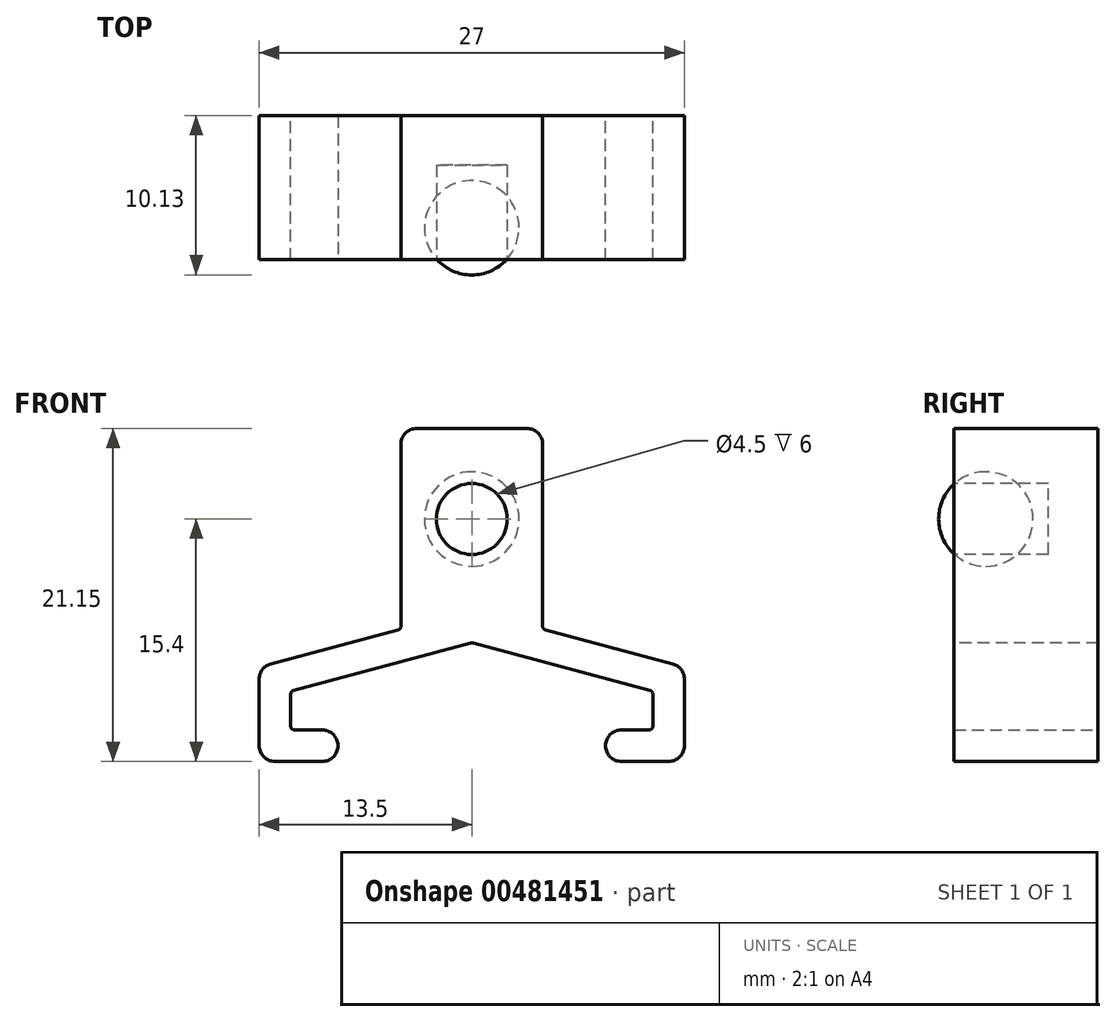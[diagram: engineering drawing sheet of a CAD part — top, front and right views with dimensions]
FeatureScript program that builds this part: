
annotation { "Feature Type Name" : "Feature", "Feature Type Description" : "" }
export const myFeature = defineFeature(function(context is Context, id is Id, definition is map)
    precondition{}
    {
        {
            var Q0;
            Q0=qCreatedBy(makeId("Front.planeOp"),FACE);
            var sketch = newSketch(context, id + "F0", { "sketchPlane" : qUnion([Q0])});
            skLineSegment(sketch, "E0.bottom", {"start": v(-13.5, -3) * mm, "end": v(-8.5, -3) * mm});
            skLineSegment(sketch, "E0.left", {"start": v(-13.5, -3) * mm, "end": v(-13.5, 3) * mm});
            skLineSegment(sketch, "E0.right", {"start": v(13.5, -3) * mm, "end": v(13.5, 3) * mm});
            skPoint(sketch, "E0.middle", {"position": v(0, 0) * mm});
            skLineSegment(sketch, "E1.top", {"start": v(4.5, 18.15) * mm, "end": v(-4.5, 18.15) * mm});
            skLineSegment(sketch, "E1.left", {"start": v(4.5, 5.4) * mm, "end": v(4.5, 18.15) * mm});
            skLineSegment(sketch, "E1.right", {"start": v(-4.5, 5.4) * mm, "end": v(-4.5, 18.15) * mm});
            skPoint(sketch, "E1.middle", {"position": v(0, 11.78) * mm});
            skLineSegment(sketch, "E2", {"start": v(4.5, 5.4) * mm, "end": v(13.5, 3) * mm});
            skLineSegment(sketch, "E3", {"start": v(-13.5, 3) * mm, "end": v(-4.5, 5.4) * mm});
            skLineSegment(sketch, "E4.0", {"start": v(-11.5, -1) * mm, "end": v(-8.5, -1) * mm});
            skLineSegment(sketch, "E5.0", {"start": v(-11.5, -1) * mm, "end": v(-11.5, 1.46) * mm});
            skLineSegment(sketch, "E6.0", {"start": v(-11.5, 1.46) * mm, "end": v(0, 4.53) * mm});
            skLineSegment(sketch, "E7.0", {"start": v(0, 4.53) * mm, "end": v(11.5, 1.46) * mm});
            skLineSegment(sketch, "E8.0", {"start": v(11.5, -1) * mm, "end": v(11.5, 1.46) * mm});
            skLineSegment(sketch, "E9", {"start": v(-8.5, -1) * mm, "end": v(-8.5, -3) * mm});
            skLineSegment(sketch, "E10.MirrorCS", {"start": v(8.5, -1) * mm, "end": v(8.5, -3) * mm});
            skLineSegment(sketch, "E11.trimOffspring", {"start": v(8.5, -1) * mm, "end": v(11.5, -1) * mm});
            skLineSegment(sketch, "E12.trimOffspring", {"start": v(8.5, -3) * mm, "end": v(13.5, -3) * mm});
            skSolve(sketch);
        }
        {
            var Q0;
            Q0=makeQuery(id+"F0.imprint","IMPRINT",FACE,{"disambiguationData":[TD([[makeQuery(id+"F0.imprint","IMPRINT",EDGE,{"derivedFrom":sQuery(id+"F0.wireOp",EDGE,"E0.bottom")}),1.0]])]});
            extrude(context, id + "F1", {"entities" : qUnion([Q0]), "depth" : 4.58 * mm, "hasSecondDirection" : true, "secondDirectionOppositeDirection" : true, "secondDirectionDepth" : 4.58 * mm});
        }
        {
            var Q0;
            Q0=makeQuery(id+"F1.opExtrude","CAP_FACE",FACE,{"disambiguationData":[OSD([sQuery(id+"F0.wireOp",EDGE,"E0.bottom"),sQuery(id+"F0.wireOp",EDGE,"E0.left"),sQuery(id+"F0.wireOp",EDGE,"E0.right"),sQuery(id+"F0.wireOp",EDGE,"E1.top"),sQuery(id+"F0.wireOp",EDGE,"E1.left"),sQuery(id+"F0.wireOp",EDGE,"E1.right"),sQuery(id+"F0.wireOp",EDGE,"E2"),sQuery(id+"F0.wireOp",EDGE,"E3"),sQuery(id+"F0.wireOp",EDGE,"E4.0"),sQuery(id+"F0.wireOp",EDGE,"E5.0"),sQuery(id+"F0.wireOp",EDGE,"E6.0"),sQuery(id+"F0.wireOp",EDGE,"E7.0"),sQuery(id+"F0.wireOp",EDGE,"E8.0"),sQuery(id+"F0.wireOp",EDGE,"E9"),sQuery(id+"F0.wireOp",EDGE,"E10.MirrorCS"),sQuery(id+"F0.wireOp",EDGE,"E11.trimOffspring"),sQuery(id+"F0.wireOp",EDGE,"E12.trimOffspring")])],"isStart":false});
            var sketch = newSketch(context, id + "F2", { "sketchPlane" : qUnion([Q0])});
            skCircle(sketch, "E13", {"center": v(0, 12.4) * mm, "radius": 2.25 * mm});
            skSolve(sketch);
        }
        {
            var Q0;
            Q0=makeQuery(id+"F2.imprint","IMPRINT",FACE,{"disambiguationData":[TD([[makeQuery(id+"F2.imprint","IMPRINT",EDGE,{"derivedFrom":sQuery(id+"F2.wireOp",EDGE,"E13")}),1.0]])]});
            extrude(context, id + "F3", {"entities" : qUnion([Q0]), "operationType" : NewBodyOperationType.REMOVE, "oppositeDirection" : true, "depth" : 6 * mm});
        }
        {
            var Q0;
            Q0=makeQuery(id+"F1.opExtrude","SWEPT_EDGE",EDGE,{"disambiguationData":[OSD([sQuery(id+"F0.wireOp",EDGE,"E1.top"),sQuery(id+"F0.wireOp",EDGE,"E1.right")])]});
            var Q1;
            Q1=makeQuery(id+"F1.opExtrude","SWEPT_EDGE",EDGE,{"disambiguationData":[OSD([sQuery(id+"F0.wireOp",EDGE,"E1.top"),sQuery(id+"F0.wireOp",EDGE,"E1.left")])]});
            var Q2;
            Q2=makeQuery(id+"F1.opExtrude","SWEPT_EDGE",EDGE,{"disambiguationData":[OSD([sQuery(id+"F0.wireOp",EDGE,"E0.right"),sQuery(id+"F0.wireOp",EDGE,"E2")])]});
            var Q3;
            Q3=makeQuery(id+"F1.opExtrude","SWEPT_EDGE",EDGE,{"disambiguationData":[OSD([sQuery(id+"F0.wireOp",EDGE,"E0.right"),sQuery(id+"F0.wireOp",EDGE,"E12.trimOffspring")])]});
            var Q4;
            Q4=makeQuery(id+"F1.opExtrude","SWEPT_EDGE",EDGE,{"disambiguationData":[OSD([sQuery(id+"F0.wireOp",EDGE,"E10.MirrorCS"),sQuery(id+"F0.wireOp",EDGE,"E12.trimOffspring")])]});
            var Q5;
            Q5=makeQuery(id+"F1.opExtrude","SWEPT_EDGE",EDGE,{"disambiguationData":[OSD([sQuery(id+"F0.wireOp",EDGE,"E10.MirrorCS"),sQuery(id+"F0.wireOp",EDGE,"E11.trimOffspring")])]});
            var Q6;
            Q6=makeQuery(id+"F1.opExtrude","SWEPT_EDGE",EDGE,{"disambiguationData":[OSD([sQuery(id+"F0.wireOp",EDGE,"E0.bottom"),sQuery(id+"F0.wireOp",EDGE,"E9")])]});
            var Q7;
            Q7=makeQuery(id+"F1.opExtrude","SWEPT_EDGE",EDGE,{"disambiguationData":[OSD([sQuery(id+"F0.wireOp",EDGE,"E4.0"),sQuery(id+"F0.wireOp",EDGE,"E9")])]});
            var Q8;
            Q8=makeQuery(id+"F1.opExtrude","SWEPT_EDGE",EDGE,{"disambiguationData":[OSD([sQuery(id+"F0.wireOp",EDGE,"E0.left"),sQuery(id+"F0.wireOp",EDGE,"E3")])]});
            var Q9;
            Q9=makeQuery(id+"F1.opExtrude","SWEPT_EDGE",EDGE,{"disambiguationData":[OSD([sQuery(id+"F0.wireOp",EDGE,"E0.bottom"),sQuery(id+"F0.wireOp",EDGE,"E0.left")])]});
            fillet(context, id + "F4", {"entities" : qUnion([Q0, Q1, Q2, Q3, Q4, Q5, Q6, Q7, Q8, Q9]), "radius" : 1 * mm, "tangentPropagation" : true, "allowEdgeOverflow" : false});
        }
        {
            var Q0;
            Q0=makeQuery(id+"F1.opExtrude","SWEPT_EDGE",EDGE,{"disambiguationData":[OSD([sQuery(id+"F0.wireOp",EDGE,"E1.left"),sQuery(id+"F0.wireOp",EDGE,"E2")])]});
            var Q1;
            Q1=makeQuery(id+"F1.opExtrude","SWEPT_EDGE",EDGE,{"disambiguationData":[OSD([sQuery(id+"F0.wireOp",EDGE,"E4.0"),sQuery(id+"F0.wireOp",EDGE,"E5.0")])]});
            var Q2;
            Q2=makeQuery(id+"F1.opExtrude","SWEPT_EDGE",EDGE,{"disambiguationData":[OSD([sQuery(id+"F0.wireOp",EDGE,"E5.0"),sQuery(id+"F0.wireOp",EDGE,"E6.0")])]});
            var Q3;
            Q3=makeQuery(id+"F1.opExtrude","SWEPT_EDGE",EDGE,{"disambiguationData":[OSD([sQuery(id+"F0.wireOp",EDGE,"E8.0"),sQuery(id+"F0.wireOp",EDGE,"E11.trimOffspring")])]});
            var Q4;
            Q4=makeQuery(id+"F1.opExtrude","SWEPT_EDGE",EDGE,{"disambiguationData":[OSD([sQuery(id+"F0.wireOp",EDGE,"E7.0"),sQuery(id+"F0.wireOp",EDGE,"E8.0")])]});
            var Q5;
            Q5=makeQuery(id+"F1.opExtrude","SWEPT_EDGE",EDGE,{"disambiguationData":[OSD([sQuery(id+"F0.wireOp",EDGE,"E6.0"),sQuery(id+"F0.wireOp",EDGE,"E7.0")])]});
            var Q6;
            Q6=makeQuery(id+"F1.opExtrude","SWEPT_EDGE",EDGE,{"disambiguationData":[OSD([sQuery(id+"F0.wireOp",EDGE,"E1.right"),sQuery(id+"F0.wireOp",EDGE,"E3")])]});
            fillet(context, id + "F5", {"entities" : qUnion([Q0, Q1, Q2, Q3, Q4, Q5, Q6]), "radius" : .25 * mm, "tangentPropagation" : true, "allowEdgeOverflow" : false});
        }
        {
            var Q0;
            Q0=qCreatedBy(makeId("Front.planeOp"),FACE);
            cPlane(context, id + "F6", {"entities" : qUnion([Q0]), "cplaneType" : CPlaneType.OFFSET, "offset" : 2.55 * mm, "width" : 150 * mm, "height" : 150 * mm});
        }
        {
            var Q0;
            Q0=qCreatedBy(id+"F6.planeOp",FACE);
            var sketch = newSketch(context, id + "F7", { "sketchPlane" : qUnion([Q0])});
            skArc(sketch, "E14", {"start": v(0, 9.4) * mm, "mid": v(3, 12.4) * mm, "end": v(0, 15.4) * mm});
            skLineSegment(sketch, "E15", {"start": v(0, 15.4) * mm, "end": v(0, 9.4) * mm});
            skSolve(sketch);
        }
        {
            var Q0;
            Q0=qSketchRegion(id+"F7",true);
            var Q1;
            Q1=sQuery(id+"F7.wireOp",EDGE,"E15");
            revolve(context, id + "F8", {"entities" : qUnion([Q0]), "axis" : qUnion([Q1]), "revolveType" : RevolveType.FULL});
        }
    });
